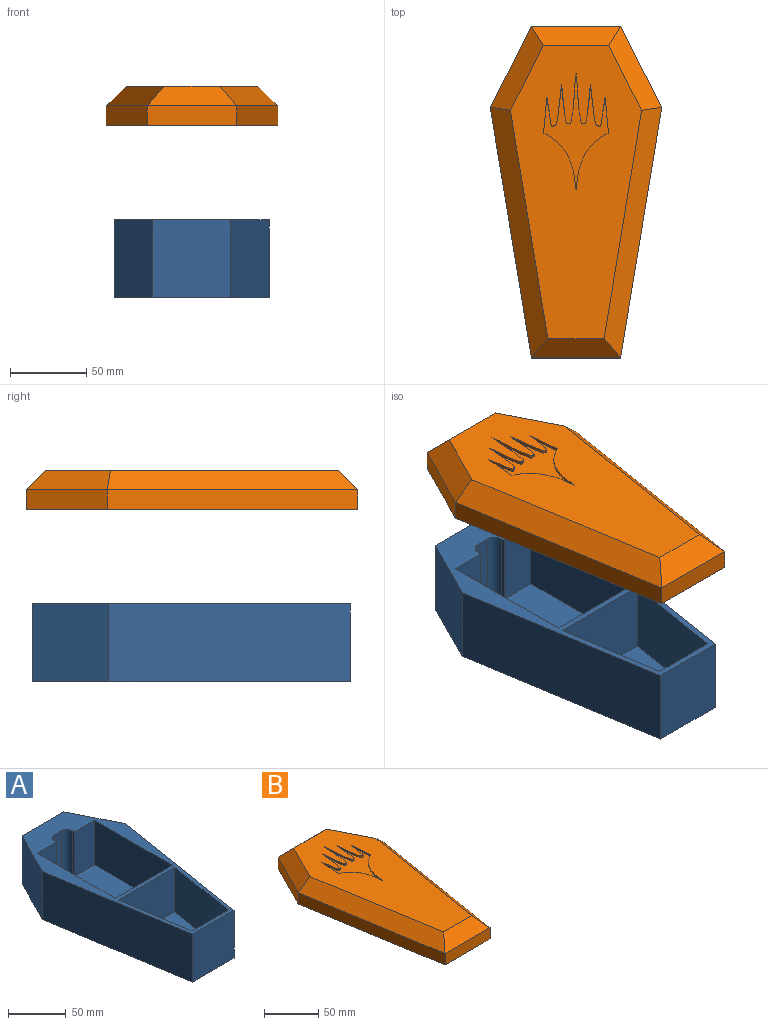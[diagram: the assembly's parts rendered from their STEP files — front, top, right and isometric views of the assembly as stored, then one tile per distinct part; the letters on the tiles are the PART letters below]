
ASSEMBLY  parts=2 mates=1
PART A: 24 faces, bbox 101.3x208.6x50.8 mm
  f0: plane 46.99x24.66mm, normal (0,-1,0), area 1159mm2, adj f1,f9,f13,f16
  f1: plane 208.58x101.31mm, normal (0,0,1), area 4619.4mm2, adj f0,f2,f3,f4,f5,f6,f7,f9
  f2: plane 50.8x50.39mm, normal (0.89,0.45,0), area 2863.4mm2, adj f1,f3,f7,f8
  f3: plane 50.8x50.8mm, normal (0,1,0), area 2580.6mm2, adj f1,f2,f4,f8
  f4: plane 50.8x50.39mm, normal (-0.89,0.45,0), area 2863.4mm2, adj f1,f3,f5,f8
  f5: plane 158.19x50.8mm, normal (-0.99,-0.16,0), area 8137.6mm2, adj f1,f4,f6,f8
  f6: plane 50.8x50.8mm, normal (0,-1,0), area 2580.6mm2, adj f1,f5,f7,f8
  f7: plane 158.19x50.8mm, normal (0.99,-0.16,0), area 8137.6mm2, adj f1,f2,f6,f8
  f8: plane 208.58x101.31mm, normal (0,0,-1), area 15863.6mm2, adj f2,f3,f4,f5,f6,f7
  f9: plane 95.25x46.99mm, normal (-1,0,0), area 4475.8mm2, adj f0,f1,f12,f13
  f10: plane 46.99x23.6mm, normal (0,-1,0), area 1108.8mm2, adj f1,f11,f13,f15
  f11: plane 95.25x46.99mm, normal (1,0,0), area 4475.8mm2, adj f1,f10,f12,f13
  f12: plane 69.85x46.99mm, normal (0,1,0), area 3282.3mm2, adj f1,f9,f11,f13
  f13: plane 104.14x69.85mm, normal (0,0,1), area 6827.8mm2, adj f0,f9,f10,f11,f12,f14,f15,f16
  f14: cylinder r=6.35mm len=46.99mm, axis (0,0,1), area 468.7mm2, adj f1,f13,f15,f18
  f15: plane 46.99x2.54mm, normal (1,0,0), area 119.4mm2, adj f1,f10,f13,f14
  f16: plane 46.99x2.54mm, normal (-1,0,0), area 119.4mm2, adj f0,f1,f13,f17
  f17: cylinder r=6.35mm len=46.99mm, axis (0,0,1), area 468.7mm2, adj f1,f13,f16,f18
  f18: plane 46.99x8.89mm, normal (0,-1,0), area 417.7mm2, adj f1,f13,f14,f17
  f19: plane 77.85x46.99mm, normal (-0.99,0.16,0), area 3704.5mm2, adj f1,f20,f22,f23
  f20: plane 69.16x46.99mm, normal (0,-1,0), area 3249.8mm2, adj f1,f19,f21,f23
  f21: plane 77.85x46.99mm, normal (0.99,0.16,0), area 3704.5mm2, adj f1,f20,f22,f23
  f22: plane 46.99x44.3mm, normal (0,1,0), area 2081.7mm2, adj f1,f19,f21,f23
  f23: plane 77.85x69.16mm, normal (0,0,1), area 4416.4mm2, adj f19,f20,f21,f22
PART B: 44 faces, bbox 112.3x217.4x25.4 mm
  f0: plane 192.02x85.94mm, normal (0,0,1), area 10920.5mm2, adj f8,f9,f10,f11,f12,f13,f27,f28
  f1: plane 53.25x26.96mm, normal (0.89,0.45,0), area 758.1mm2, adj f2,f6,f7,f10
  f2: plane 58.42x12.7mm, normal (0,1,0), area 741.9mm2, adj f1,f3,f7,f8
  f3: plane 53.25x26.96mm, normal (-0.89,0.45,0), area 758.1mm2, adj f2,f4,f7,f9
  f4: plane 164.17x26.96mm, normal (-0.99,-0.16,0), area 2112.9mm2, adj f3,f5,f7,f11
  f5: plane 58.42x12.7mm, normal (0,-1,0), area 741.9mm2, adj f4,f6,f7,f13
  f6: plane 164.17x26.96mm, normal (0.99,-0.16,0), area 2112.9mm2, adj f1,f5,f7,f12
  f7: plane 217.42x112.35mm, normal (0,0,-1), area 716.8mm2, adj f1,f2,f3,f4,f5,f6,f38,f39
  f8: plane 58.42x12.7mm, normal (0,0.71,0.71), area 909.1mm2, adj f0,f2,f9,f10
  f9: plane 55.29x34.77mm, normal (-0.63,0.32,0.71), area 964.7mm2, adj f0,f3,f8,f11
  f10: plane 55.29x34.77mm, normal (0.63,0.32,0.71), area 964.7mm2, adj f0,f1,f8,f12
  f11: plane 164.17x37.75mm, normal (-0.7,-0.11,0.71), area 2854mm2, adj f0,f4,f9,f13
  f12: plane 164.17x37.75mm, normal (0.7,-0.11,0.71), area 2854mm2, adj f0,f6,f10,f13
  f13: plane 58.42x12.7mm, normal (0,-0.71,0.71), area 855.6mm2, adj f0,f5,f11,f12
  f14: plane 50.05x25.34mm, normal (-0.89,-0.45,0), area 481.5mm2, adj f15,f19,f23,f39
  f15: plane 53.74x8.58mm, normal (0,-1,0), area 461.2mm2, adj f14,f16,f21,f41
  f16: plane 50.05x25.34mm, normal (0.89,-0.45,0), area 481.5mm2, adj f15,f17,f22,f43
  f17: plane 159.75x26.24mm, normal (0.99,0.16,0), area 1389.3mm2, adj f16,f18,f24,f42
  f18: plane 51.95x8.58mm, normal (0,1,0), area 445.8mm2, adj f17,f19,f26,f40
  f19: plane 159.75x26.24mm, normal (-0.99,0.16,0), area 1389.3mm2, adj f14,f18,f25,f38
  f20: plane 188.87x82.65mm, normal (0,0,-1), area 11170.5mm2, adj f21,f22,f23,f24,f25,f26
  f21: plane 53.74x10.47mm, normal (0,-0.71,-0.71), area 700.3mm2, adj f15,f20,f22,f23
  f22: plane 51.73x31.78mm, normal (0.63,-0.32,-0.71), area 757.6mm2, adj f16,f20,f21,f24
  f23: plane 51.73x31.78mm, normal (-0.63,-0.32,-0.71), area 757.6mm2, adj f14,f20,f21,f25
  f24: plane 159.75x35.13mm, normal (0.7,0.11,-0.71), area 2305.5mm2, adj f17,f20,f22,f26
  f25: plane 159.75x35.13mm, normal (-0.7,0.11,-0.71), area 2305.5mm2, adj f19,f20,f23,f26
  f26: plane 51.95x10.47mm, normal (0,0.71,-0.71), area 637.5mm2, adj f18,f20,f24,f25
  f27: extruded ~36.9x21.31mm, area 86.1mm2, adj f0,f28,f36,f37
  f28: extruded ~36.9x21.31mm, area 86.1mm2, adj f0,f27,f29,f37
  f29: plane 23.35x2.22mm, normal (-1,-0.09,0), area 44.7mm2, adj f0,f28,f30,f37
  f30: extruded ~27.17x12.75mm, area 144.7mm2, adj f0,f29,f31,f37
  f31: extruded ~1.91x0.7mm, area 1.3mm2, adj f0,f30,f32,f37
  f32: extruded ~32.82x5.66mm, area 66.8mm2, adj f0,f31,f33,f37
  f33: extruded ~32.82x5.66mm, area 66.8mm2, adj f0,f32,f34,f37
  f34: extruded ~1.91x0.7mm, area 1.3mm2, adj f0,f33,f35,f37
  f35: extruded ~27.17x12.75mm, area 144.7mm2, adj f0,f34,f36,f37
  f36: plane 23.35x2.22mm, normal (1,-0.09,0), area 44.7mm2, adj f0,f27,f35,f37
  f37: plane 76.35x42.63mm, normal (0,0,1), area 995.5mm2, adj f27,f28,f29,f30,f31,f32,f33,f34
  f38: plane 162.7x28.88mm, normal (-0.7,0.11,-0.71), area 586.9mm2, adj f7,f19,f39,f40
  f39: plane 52.59x27.98mm, normal (-0.63,-0.32,-0.71), area 205.8mm2, adj f7,f14,f38,f41
  f40: plane 56.26x2.54mm, normal (0,0.71,-0.71), area 194.4mm2, adj f7,f18,f38,f42
  f41: plane 56.86x2.54mm, normal (0,-0.71,-0.71), area 198.6mm2, adj f7,f15,f39,f43
  f42: plane 162.7x28.88mm, normal (0.7,0.11,-0.71), area 586.9mm2, adj f7,f17,f40,f43
  f43: plane 52.59x27.98mm, normal (0.63,-0.32,-0.71), area 205.8mm2, adj f7,f16,f41,f42
PLACE A t=(-4.87,24.35,16.99)mm
PLACE B t=(-4.57,0,129.79)mm
MATE parallel A.f6 <-> B.f18  axis (0,-1,0) through (-4.72,-99.59,42.39)mm
